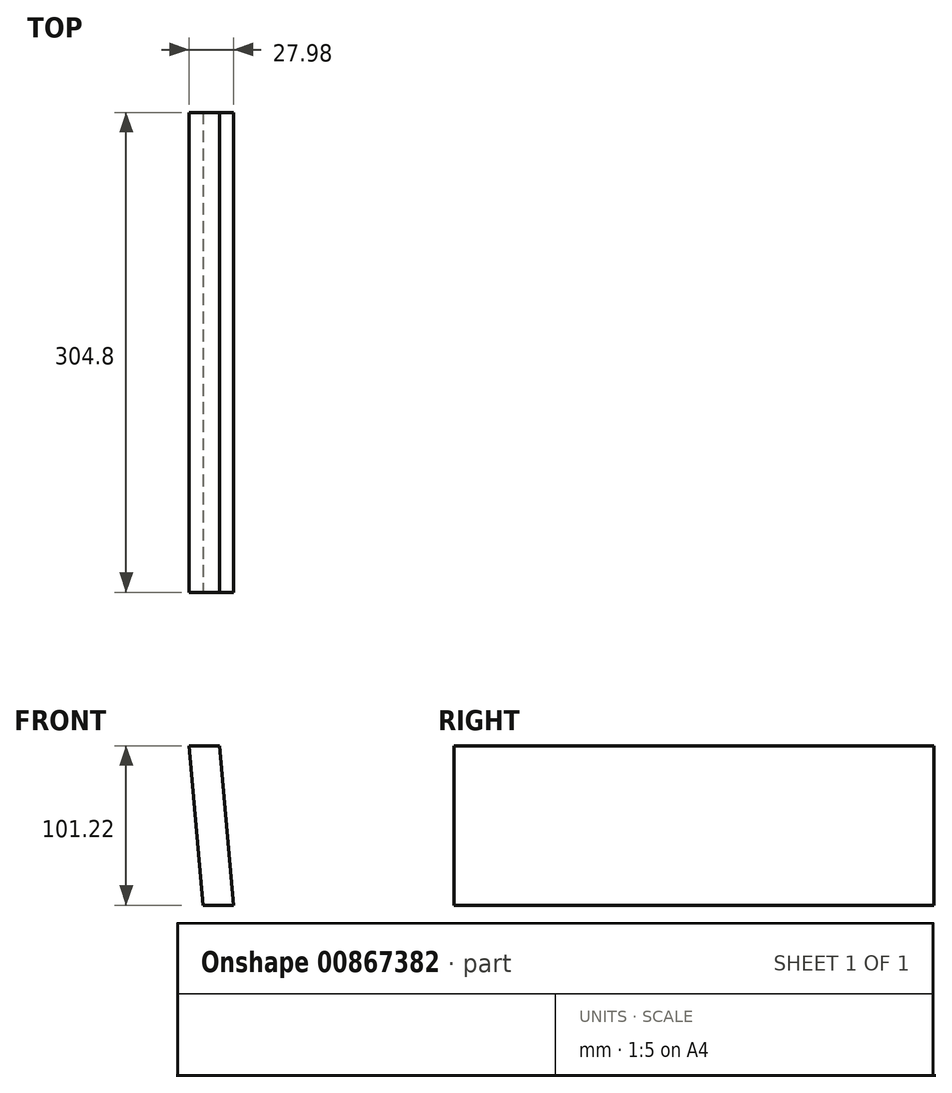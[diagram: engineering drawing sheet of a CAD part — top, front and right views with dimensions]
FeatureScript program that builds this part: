
annotation { "Feature Type Name" : "Feature", "Feature Type Description" : "" }
export const myFeature = defineFeature(function(context is Context, id is Id, definition is map)
    precondition{}
    {
        {
            var Q0;
            Q0=qCreatedBy(makeId("Front.planeOp"),FACE);
            var sketch = newSketch(context, id + "F0", { "sketchPlane" : qUnion([Q0])});
            skLineSegment(sketch, "E0", {"start": v(-14.11, 48.22) * mm, "end": v(-5.26, -53) * mm});
            skLineSegment(sketch, "E1", {"start": v(5.01, 48.22) * mm, "end": v(13.87, -53) * mm});
            skLineSegment(sketch, "E2", {"start": v(-14.11, 48.22) * mm, "end": v(5.01, 48.22) * mm});
            skLineSegment(sketch, "E3", {"start": v(-5.26, -53) * mm, "end": v(13.87, -53) * mm});
            skSolve(sketch);
        }
        {
            var Q0;
            Q0=sQuery(id+"F0.wireOp",EDGE,"E2");
            var Q1;
            Q1=sQuery(id+"F0.wireOp",EDGE,"E0");
            var Q2;
            Q2=sQuery(id+"F0.wireOp",EDGE,"E1");
            var Q3;
            Q3=sQuery(id+"F0.wireOp",EDGE,"E3");
            extrude(context, id + "F1", {"bodyType" : ToolBodyType.SURFACE, "surfaceEntities" : qUnion([Q0, Q1, Q2, Q3]), "depth" : 304.8 * mm, "offsetDistance" : 25.4 * mm});
        }
    });
